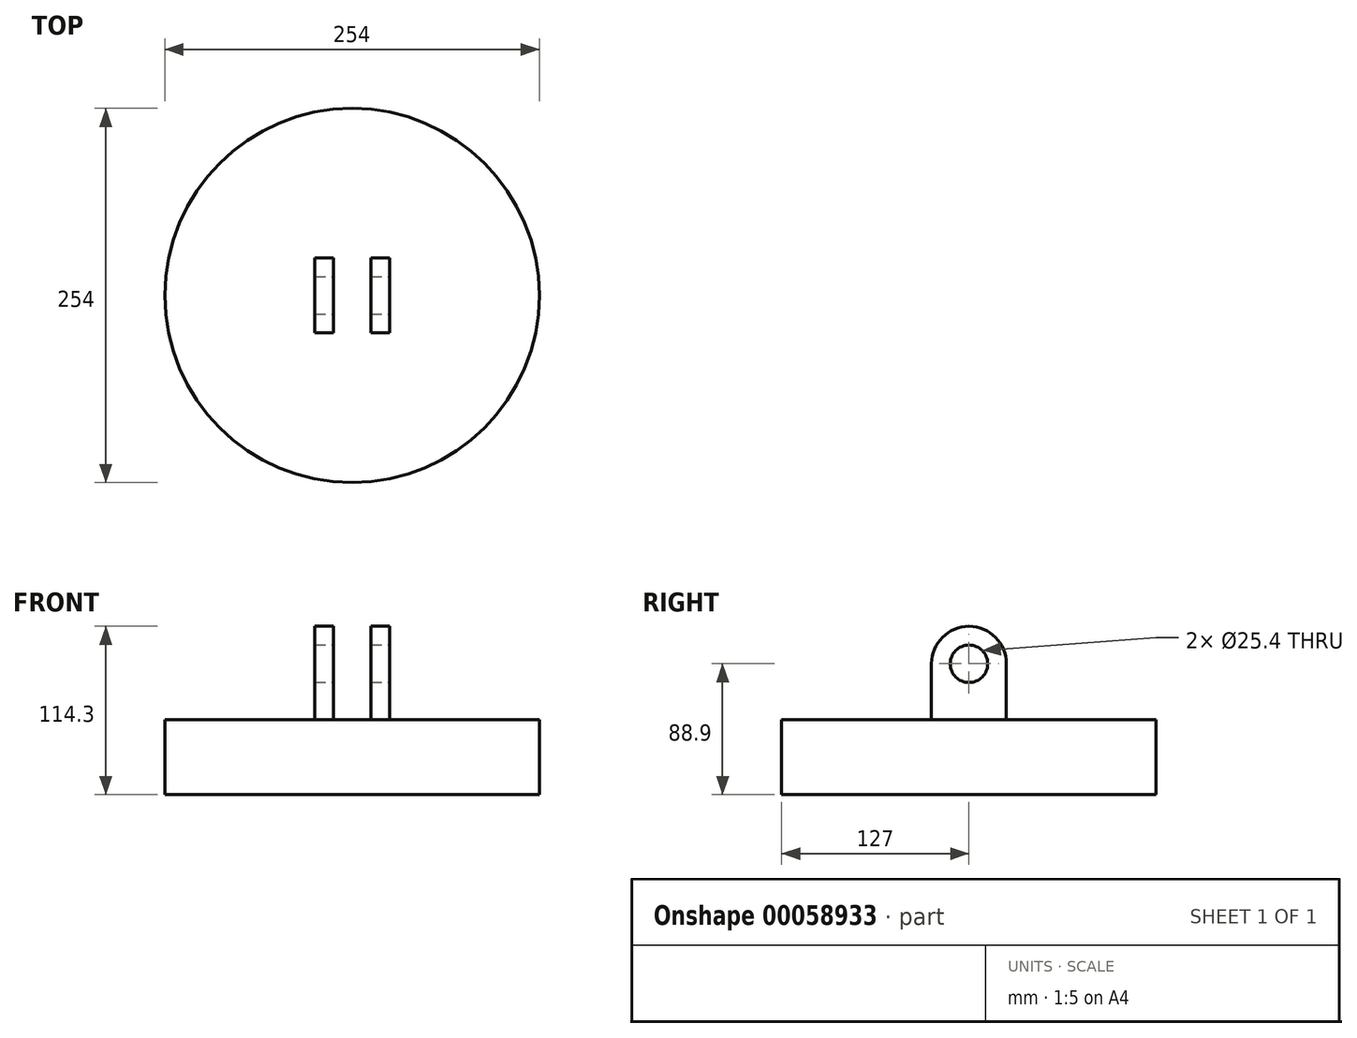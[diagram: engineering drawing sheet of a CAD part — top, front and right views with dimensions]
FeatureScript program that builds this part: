
annotation { "Feature Type Name" : "Feature", "Feature Type Description" : "" }
export const myFeature = defineFeature(function(context is Context, id is Id, definition is map)
    precondition{}
    {
        {
            var Q0;
            Q0=qCreatedBy(makeId("Front.planeOp"),FACE);
            var sketch = newSketch(context, id + "F0", { "sketchPlane" : qUnion([Q0])});
            skLineSegment(sketch, "E0", {"start": v(0, 0) * mm, "end": v(0, 50.8) * mm});
            skLineSegment(sketch, "E1", {"start": v(127, 0) * mm, "end": v(0, 0) * mm});
            skLineSegment(sketch, "E2", {"start": v(0, 50.8) * mm, "end": v(127, 50.8) * mm});
            skLineSegment(sketch, "E3", {"start": v(127, 0) * mm, "end": v(127, 50.8) * mm});
            skSolve(sketch);
        }
        {
            var Q0;
            Q0 = qSketchRegion(id + "F0", true);
            var Q1;
            Q1=sQuery(id+"F0.wireOp",EDGE,"E0");
            revolve(context, id + "F1", {"entities" : qUnion([Q0]), "axis" : qUnion([Q1]), "revolveType" : RevolveType.FULL});
        }
        {
            var Q0;
            Q0=qCreatedBy(makeId("Right.planeOp"),FACE);
            var sketch = newSketch(context, id + "F2", { "sketchPlane" : qUnion([Q0])});
            skLineSegment(sketch, "E4.0", {"start": v(127, 50.8) * mm, "end": v(-127, 50.8) * mm, "construction": true});
            skLineSegment(sketch, "E5", {"start": v(-25.4, 50.8) * mm, "end": v(-25.4, 88.9) * mm});
            skLineSegment(sketch, "E6", {"start": v(-25.4, 88.9) * mm, "end": v(25.4, 88.9) * mm, "construction": true});
            skLineSegment(sketch, "E7", {"start": v(25.4, 88.9) * mm, "end": v(25.4, 50.8) * mm});
            skLineSegment(sketch, "E8", {"start": v(0, 50.8) * mm, "end": v(0, 88.9) * mm, "construction": true});
            skArc(sketch, "E9", {"start": v(-25.4, 88.9) * mm, "mid": v(0, 114.3) * mm, "end": v(25.4, 88.9) * mm});
            skLineSegment(sketch, "E10", {"start": v(-25.4, 50.8) * mm, "end": v(25.4, 50.8) * mm});
            skSolve(sketch);
        }
        {
            var Q0;
            Q0 = qSketchRegion(id + "F2", true);
            extrude(context, id + "F3", {"entities" : qUnion([Q0]), "operationType" : NewBodyOperationType.ADD, "endBound" : BoundingType.SYMMETRIC, "depth" : 50.8 * mm});
        }
        {
            var Q0;
            Q0=makeQuery(id+"F3.opExtrude","SWEPT_FACE",FACE,{"disambiguationData":[OSD([sQuery(id+"F2.wireOp",EDGE,"E7")])]});
            var sketch = newSketch(context, id + "F4", { "sketchPlane" : qUnion([Q0])});
            skLineSegment(sketch, "E11", {"start": v(-12.7, 50.8) * mm, "end": v(12.7, 50.8) * mm});
            skLineSegment(sketch, "E12", {"start": v(12.7, 50.8) * mm, "end": v(12.7, 152.4) * mm});
            skLineSegment(sketch, "E13", {"start": v(12.7, 152.4) * mm, "end": v(-12.7, 152.4) * mm});
            skLineSegment(sketch, "E14", {"start": v(-12.7, 152.4) * mm, "end": v(-12.7, 50.8) * mm});
            skLineSegment(sketch, "E15", {"start": v(0, 50.8) * mm, "end": v(0, 152.4) * mm, "construction": true});
            skSolve(sketch);
        }
        {
            var Q0;
            Q0 = qSketchRegion(id + "F4", true);
            var Q1;
            Q1=sQuery(id+"F4.wireOp",EDGE,"E15");
            extrude(context, id + "F5", {"entities" : qUnion([Q0]), "operationType" : NewBodyOperationType.REMOVE, "surfaceEntities" : qUnion([Q1]), "endBound" : BoundingType.THROUGH_ALL, "oppositeDirection" : true, "depth" : 25.4 * mm});
        }
        {
            var Q0;
            Q0=makeQuery(id+"F3.opExtrude","CAP_FACE",FACE,{"disambiguationData":[OSD([sQuery(id+"F2.wireOp",EDGE,"E5"),sQuery(id+"F2.wireOp",EDGE,"E7"),sQuery(id+"F2.wireOp",EDGE,"E9"),sQuery(id+"F2.wireOp",EDGE,"E10")])],"isStart":false});
            var sketch = newSketch(context, id + "F6", { "sketchPlane" : qUnion([Q0])});
            skCircle(sketch, "E16", {"center": v(0, 88.9) * mm, "radius": 12.7 * mm});
            skSolve(sketch);
        }
        {
            var Q0;
            Q0 = qSketchRegion(id + "F6", true);
            extrude(context, id + "F7", {"entities" : qUnion([Q0]), "operationType" : NewBodyOperationType.REMOVE, "endBound" : BoundingType.THROUGH_ALL, "oppositeDirection" : true, "depth" : 25.4 * mm});
        }
    });
